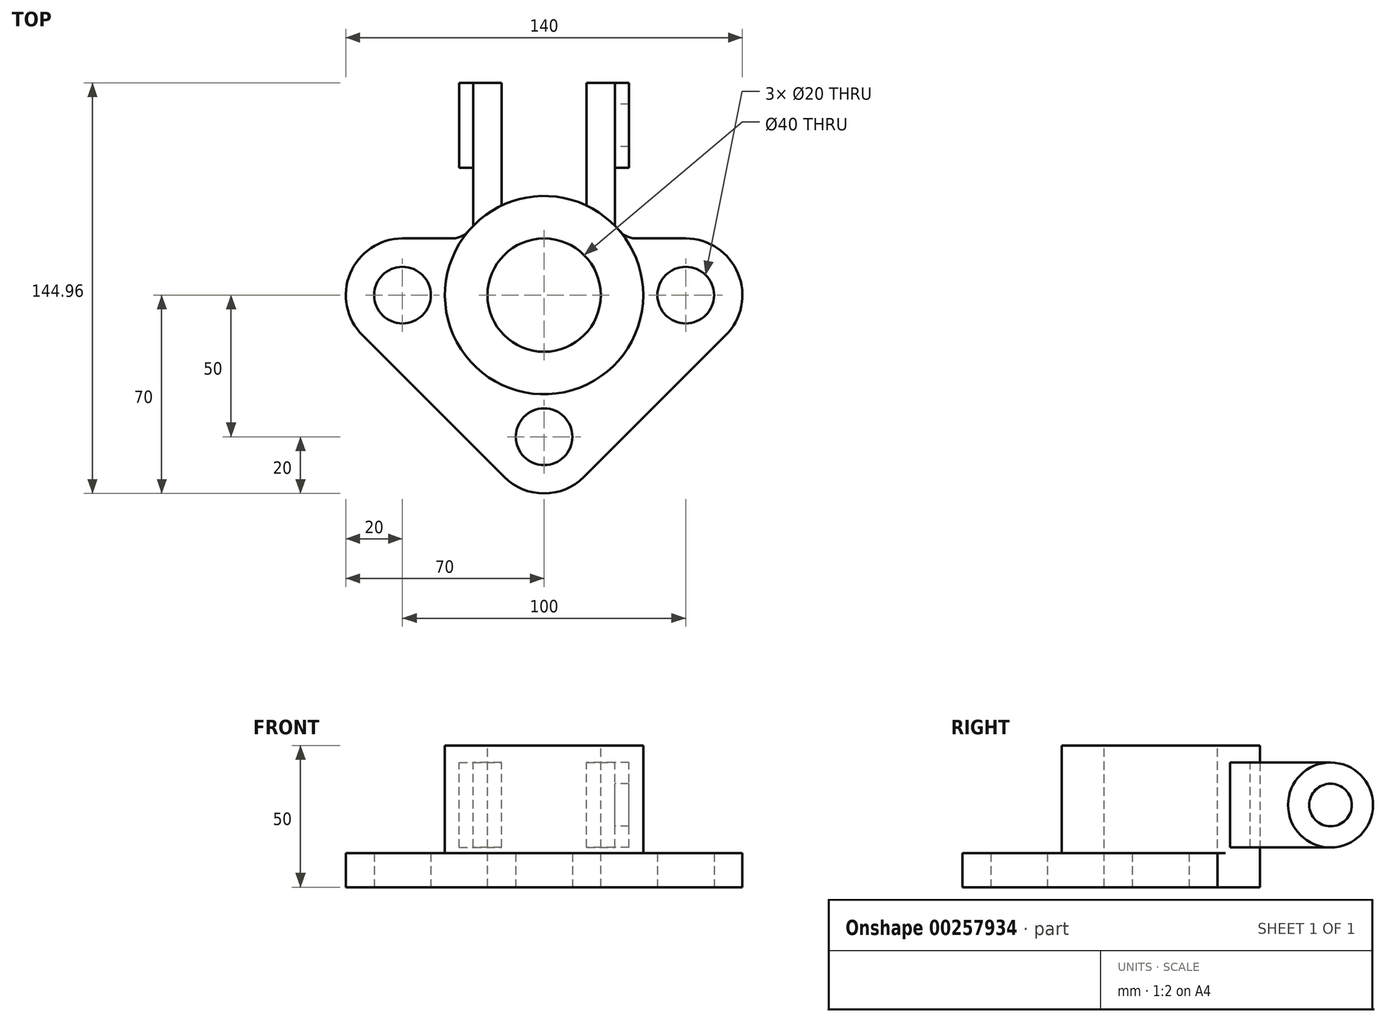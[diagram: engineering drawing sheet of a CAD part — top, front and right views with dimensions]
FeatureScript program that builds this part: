
annotation { "Feature Type Name" : "Feature", "Feature Type Description" : "" }
export const myFeature = defineFeature(function(context is Context, id is Id, definition is map)
    precondition{}
    {
        {
            var Q0;
            Q0=qCreatedBy(makeId("Top.planeOp"),FACE);
            var sketch = newSketch(context, id + "F0", { "sketchPlane" : qUnion([Q0])});
            skCircle(sketch, "E0", {"center": v(-50, 0) * mm, "radius": 10 * mm});
            skCircle(sketch, "E1", {"center": v(50, 0) * mm, "radius": 10 * mm});
            skArc(sketch, "E2", {"start": v(-50, 20) * mm, "mid": v(-68.48, 7.65) * mm, "end": v(-64.14, -14.14) * mm});
            skArc(sketch, "E3", {"start": v(64.14, -14.14) * mm, "mid": v(68.48, 7.65) * mm, "end": v(50, 20) * mm});
            skCircle(sketch, "E4", {"center": v(0, -50) * mm, "radius": 10 * mm});
            skArc(sketch, "E5", {"start": v(-14.14, -64.14) * mm, "mid": v(0, -70) * mm, "end": v(14.14, -64.14) * mm});
            skArc(sketch, "E6", {"start": v(26.56, 22.8) * mm, "mid": v(0, 35) * mm, "end": v(-26.56, 22.8) * mm});
            skArc(sketch, "E7", {"start": v(26.56, 22.8) * mm, "mid": v(29.3, 20.73) * mm, "end": v(32.63, 20) * mm});
            skArc(sketch, "E8", {"start": v(-32.63, 20) * mm, "mid": v(-29.3, 20.73) * mm, "end": v(-26.56, 22.8) * mm});
            skLineSegment(sketch, "E9", {"start": v(-50, 20) * mm, "end": v(-32.63, 20) * mm});
            skLineSegment(sketch, "E10", {"start": v(-64.14, -14.14) * mm, "end": v(-14.14, -64.14) * mm});
            skLineSegment(sketch, "E11", {"start": v(14.14, -64.14) * mm, "end": v(64.14, -14.14) * mm});
            skLineSegment(sketch, "E12.trimOffspring", {"start": v(32.63, 20) * mm, "end": v(50, 20) * mm});
            skSolve(sketch);
        }
        {
            var Q0;
            Q0=makeQuery(id+"F0.imprint","IMPRINT",FACE,{"disambiguationData":[TD([[makeQuery(id+"F0.imprint","IMPRINT",EDGE,{"derivedFrom":sQuery(id+"F0.wireOp",EDGE,"E0")}),-1.0]])]});
            extrude(context, id + "F1", {"entities" : qUnion([Q0]), "depth" : 12 * mm});
        }
        {
            var Q0;
            Q0=makeQuery(id+"F1.opExtrude","CAP_FACE",FACE,{"disambiguationData":[OSD([sQuery(id+"F0.wireOp",EDGE,"E0"),sQuery(id+"F0.wireOp",EDGE,"E1"),sQuery(id+"F0.wireOp",EDGE,"E2"),sQuery(id+"F0.wireOp",EDGE,"E3"),sQuery(id+"F0.wireOp",EDGE,"E4"),sQuery(id+"F0.wireOp",EDGE,"E5"),sQuery(id+"F0.wireOp",EDGE,"E6"),sQuery(id+"F0.wireOp",EDGE,"E7"),sQuery(id+"F0.wireOp",EDGE,"E8"),sQuery(id+"F0.wireOp",EDGE,"E9"),sQuery(id+"F0.wireOp",EDGE,"E10"),sQuery(id+"F0.wireOp",EDGE,"E11"),sQuery(id+"F0.wireOp",EDGE,"E12.trimOffspring")])],"isStart":false});
            var sketch = newSketch(context, id + "F2", { "sketchPlane" : qUnion([Q0])});
            skCircle(sketch, "E13", {"center": v(0, 0) * mm, "radius": 35 * mm});
            skSolve(sketch);
        }
        {
            var Q0;
            Q0 = qSketchRegion(id + "F2", true);
            extrude(context, id + "F3", {"entities" : qUnion([Q0]), "operationType" : NewBodyOperationType.ADD, "depth" : 38 * mm});
        }
        {
            var Q0;
            Q0=makeQuery(id+"F3.opExtrude","CAP_FACE",FACE,{"disambiguationData":[OSD([sQuery(id+"F2.wireOp",EDGE,"E13")])],"isStart":false});
            var sketch = newSketch(context, id + "F4", { "sketchPlane" : qUnion([Q0])});
            skCircle(sketch, "E14", {"center": v(0, 0) * mm, "radius": 20 * mm});
            skSolve(sketch);
        }
        {
            var Q0;
            Q0=makeQuery(id+"F4.imprint","IMPRINT",FACE,{"disambiguationData":[TD([[makeQuery(id+"F4.imprint","IMPRINT",EDGE,{"derivedFrom":sQuery(id+"F4.wireOp",EDGE,"E14")}),1.0]])]});
            extrude(context, id + "F5", {"entities" : qUnion([Q0]), "oppositeDirection" : true, "depth" : 100 * mm});
        }
        {
            var Q0;
            Q0=makeQuery(id+"F5.opExtrude","SWEPT_BODY",BODY,{"disambiguationData":[OSD([sQuery(id+"F4.wireOp",EDGE,"E14")])]});
            var Q1;
            Q1=makeQuery(id+"F1.opExtrude","SWEPT_BODY",BODY,{"disambiguationData":[OSD([sQuery(id+"F0.wireOp",EDGE,"E0"),sQuery(id+"F0.wireOp",EDGE,"E1"),sQuery(id+"F0.wireOp",EDGE,"E2"),sQuery(id+"F0.wireOp",EDGE,"E3"),sQuery(id+"F0.wireOp",EDGE,"E4"),sQuery(id+"F0.wireOp",EDGE,"E5"),sQuery(id+"F0.wireOp",EDGE,"E6"),sQuery(id+"F0.wireOp",EDGE,"E7"),sQuery(id+"F0.wireOp",EDGE,"E8"),sQuery(id+"F0.wireOp",EDGE,"E9"),sQuery(id+"F0.wireOp",EDGE,"E10"),sQuery(id+"F0.wireOp",EDGE,"E11"),sQuery(id+"F0.wireOp",EDGE,"E12.trimOffspring")])]});
            booleanBodies(context, id + "F6", {"operationType" : BooleanOperationType.SUBTRACTION, "tools" : qUnion([Q0]), "targets" : qUnion([Q1])});
        }
        {
            var Q0;
            Q0=qCreatedBy(makeId("Right.planeOp"),FACE);
            var sketch = newSketch(context, id + "F7", { "sketchPlane" : qUnion([Q0])});
            skArc(sketch, "E15", {"start": v(59.96, 14) * mm, "mid": v(74.96, 29) * mm, "end": v(59.96, 44) * mm});
            skLineSegment(sketch, "E16", {"start": v(59.96, 14) * mm, "end": v(21.95, 14) * mm});
            skLineSegment(sketch, "E17", {"start": v(21.95, 14) * mm, "end": v(21.95, 44) * mm});
            skLineSegment(sketch, "E18", {"start": v(59.96, 44) * mm, "end": v(21.95, 44) * mm});
            skSolve(sketch);
        }
        {
            var Q0;
            Q0=makeQuery(id+"F7.imprint","IMPRINT",FACE,{"disambiguationData":[TD([[makeQuery(id+"F7.imprint","IMPRINT",EDGE,{"derivedFrom":sQuery(id+"F7.wireOp",EDGE,"E15")}),1.0]])]});
            var Q1;
            Q1 = qConstructionFilter(qBodyType(qCreatedBy(id + "F7" ,EDGE), BodyType.WIRE), ConstructionObject.NO);
            extrude(context, id + "F8", {"entities" : qUnion([Q0]), "surfaceEntities" : qUnion([Q1]), "endBound" : BoundingType.SYMMETRIC, "depth" : 50 * mm});
        }
        {
            var Q0;
            Q0=qCreatedBy(makeId("Right.planeOp"),FACE);
            var sketch = newSketch(context, id + "F9", { "sketchPlane" : qUnion([Q0])});
            skCircle(sketch, "E19", {"center": v(59.96, 29) * mm, "radius": 7.5 * mm});
            skSolve(sketch);
        }
        {
            var Q0;
            Q0 = qSketchRegion(id + "F9", true);
            extrude(context, id + "F10", {"entities" : qUnion([Q0]), "endBound" : BoundingType.SYMMETRIC, "depth" : 75 * mm});
        }
        {
            var Q0;
            Q0=makeQuery(id+"F3.opExtrude","CAP_FACE",FACE,{"disambiguationData":[OSD([sQuery(id+"F2.wireOp",EDGE,"E13")])],"isStart":false});
            var sketch = newSketch(context, id + "F11", { "sketchPlane" : qUnion([Q0])});
            skCircle(sketch, "E20", {"center": v(0, 0) * mm, "radius": 35 * mm});
            skCircle(sketch, "E21", {"center": v(0, 0) * mm, "radius": 20 * mm});
            skSolve(sketch);
        }
        {
            var Q0;
            Q0 = qSketchRegion(id + "F11", true);
            extrude(context, id + "F12", {"entities" : qUnion([Q0]), "oppositeDirection" : true, "depth" : 76.8 * mm});
        }
        {
            var Q0;
            Q0=makeQuery(id+"F12.opExtrude","SWEPT_BODY",BODY,{"disambiguationData":[OSD([sQuery(id+"F11.wireOp",EDGE,"E20"),sQuery(id+"F11.wireOp",EDGE,"E21")])]});
            var Q1;
            Q1=makeQuery(id+"F8.opExtrude","SWEPT_BODY",BODY,{"disambiguationData":[OSD([sQuery(id+"F7.wireOp",EDGE,"E15"),sQuery(id+"F7.wireOp",EDGE,"E16"),sQuery(id+"F7.wireOp",EDGE,"E17"),sQuery(id+"F7.wireOp",EDGE,"E18")])]});
            booleanBodies(context, id + "F13", {"operationType" : BooleanOperationType.SUBTRACTION, "tools" : qUnion([Q0]), "targets" : qUnion([Q1])});
        }
        {
            var Q0;
            Q0=makeQuery(id+"F8.opExtrude","SWEPT_FACE",FACE,{"disambiguationData":[OSD([sQuery(id+"F7.wireOp",EDGE,"E18")])]});
            var sketch = newSketch(context, id + "F14", { "sketchPlane" : qUnion([Q0])});
            skArc(sketch, "E22", {"start": v(15, 31.62) * mm, "mid": v(0, 35) * mm, "end": v(-15, 31.62) * mm});
            skLineSegment(sketch, "E23.top", {"start": v(-15, 81.54) * mm, "end": v(15, 81.54) * mm});
            skLineSegment(sketch, "E23.left", {"start": v(-15, 31.62) * mm, "end": v(-15, 81.54) * mm});
            skLineSegment(sketch, "E23.right", {"start": v(15, 31.62) * mm, "end": v(15, 81.54) * mm});
            skSolve(sketch);
        }
        {
            var Q0;
            Q0 = qSketchRegion(id + "F14", true);
            extrude(context, id + "F15", {"entities" : qUnion([Q0]), "oppositeDirection" : true, "depth" : 42.9 * mm});
        }
        {
            var Q0;
            Q0=makeQuery(id+"F15.opExtrude","SWEPT_BODY",BODY,{"disambiguationData":[OSD([sQuery(id+"F14.wireOp",EDGE,"E22"),sQuery(id+"F14.wireOp",EDGE,"E23.top"),sQuery(id+"F14.wireOp",EDGE,"E23.left"),sQuery(id+"F14.wireOp",EDGE,"E23.right")])]});
            var Q1;
            Q1=makeQuery(id+"F8.opExtrude","SWEPT_BODY",BODY,{"disambiguationData":[OSD([sQuery(id+"F7.wireOp",EDGE,"E15"),sQuery(id+"F7.wireOp",EDGE,"E16"),sQuery(id+"F7.wireOp",EDGE,"E17"),sQuery(id+"F7.wireOp",EDGE,"E18")])]});
            booleanBodies(context, id + "F16", {"operationType" : BooleanOperationType.SUBTRACTION, "tools" : qUnion([Q0]), "targets" : qUnion([Q1])});
        }
        {
            var Q0;
            Q0=makeQuery(id+"F8.opExtrude","CAP_FACE",FACE,{"disambiguationData":[OSD([sQuery(id+"F7.wireOp",EDGE,"E15"),sQuery(id+"F7.wireOp",EDGE,"E16"),sQuery(id+"F7.wireOp",EDGE,"E17"),sQuery(id+"F7.wireOp",EDGE,"E18")])],"isStart":false});
            var sketch = newSketch(context, id + "F17", { "sketchPlane" : qUnion([Q0])});
            skCircle(sketch, "E24", {"center": v(59.96, 29) * mm, "radius": 15 * mm});
            skSolve(sketch);
        }
        {
            var Q0;
            Q0 = qSketchRegion(id + "F17", true);
            extrude(context, id + "F18", {"entities" : qUnion([Q0]), "depth" : 5 * mm});
        }
        {
            var Q0;
            Q0=makeQuery(id+"F18.opExtrude","SWEPT_BODY",BODY,{"disambiguationData":[OSD([sQuery(id+"F17.wireOp",EDGE,"E24")])]});
            var Q1;
            Q1=qCreatedBy(makeId("Right.planeOp"),FACE);
            mirror(context, id + "F19", {"entities" : qUnion([Q0]), "mirrorPlane" : qUnion([Q1])});
        }
        {
            var Q0;
            Q0=makeQuery(id+"F10.opExtrude","SWEPT_BODY",BODY,{"disambiguationData":[OSD([sQuery(id+"F9.wireOp",EDGE,"E19")])]});
            var Q1;
            Q1=makeQuery(id+"F18.opExtrude","SWEPT_BODY",BODY,{"disambiguationData":[OSD([sQuery(id+"F17.wireOp",EDGE,"E24")])]});
            booleanBodies(context, id + "F20", {"operationType" : BooleanOperationType.SUBTRACTION, "tools" : qUnion([Q0]), "targets" : qUnion([Q1])});
        }
    });
